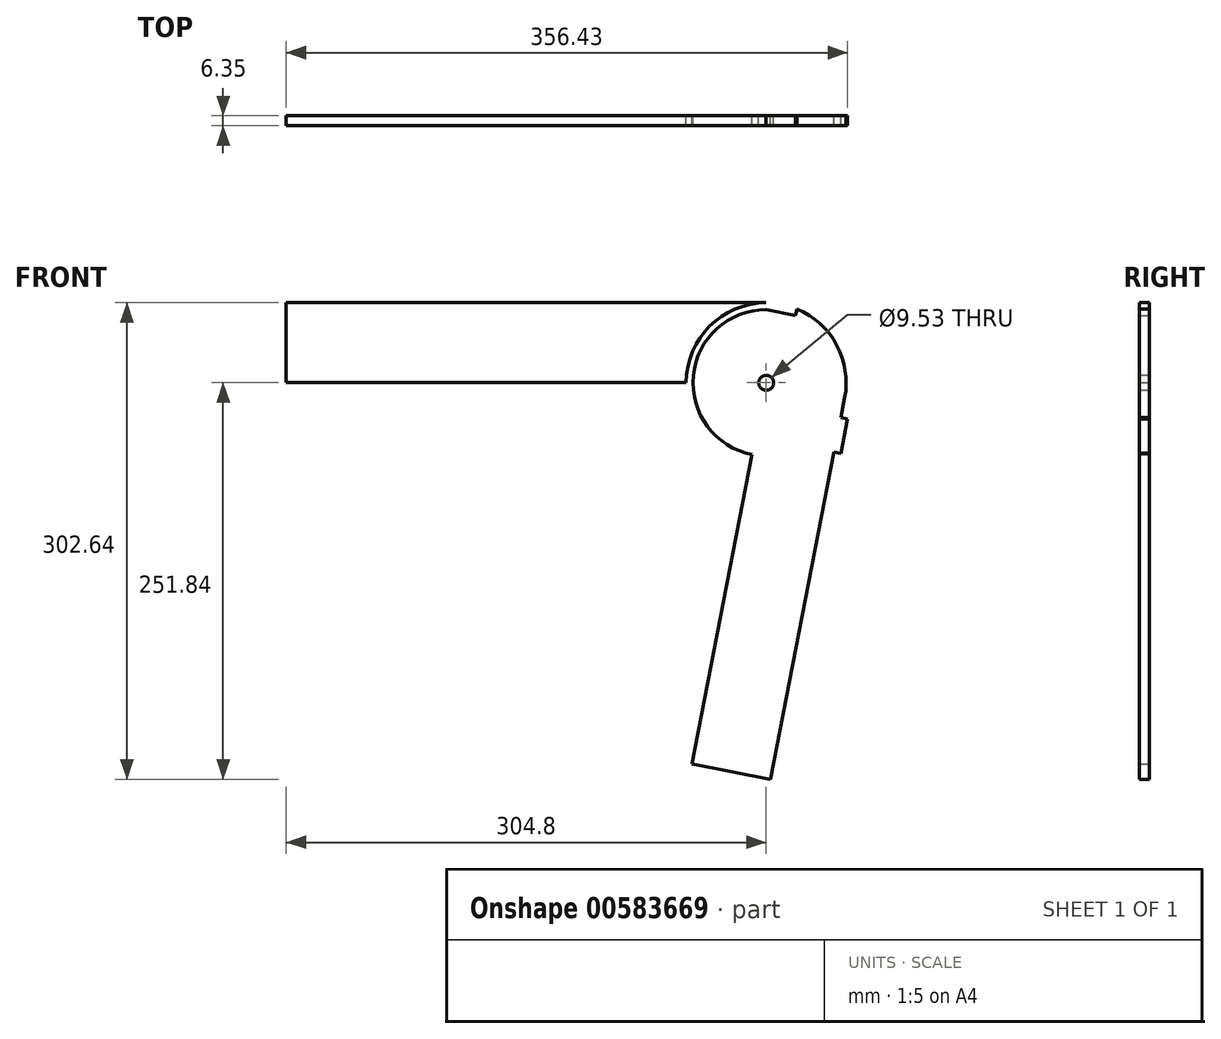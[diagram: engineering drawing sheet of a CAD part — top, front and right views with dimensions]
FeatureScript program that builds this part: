
annotation { "Feature Type Name" : "Feature", "Feature Type Description" : "" }
export const myFeature = defineFeature(function(context is Context, id is Id, definition is map)
    precondition{}
    {
        {
            var Q0;
            Q0=qCreatedBy(makeId("Front.planeOp"),FACE);
            var sketch = newSketch(context, id + "F0", { "sketchPlane" : qUnion([Q0])});
            skCircle(sketch, "E0", {"center": v(0, 0) * mm, "radius": 50.8 * mm});
            skLineSegment(sketch, "E1", {"start": v(0, 50.8) * mm, "end": v(-304.8, 50.8) * mm});
            skLineSegment(sketch, "E2", {"start": v(-304.8, 50.8) * mm, "end": v(-304.8, 0) * mm});
            skLineSegment(sketch, "E3", {"start": v(-304.8, 0) * mm, "end": v(-50.8, 0) * mm});
            skCircle(sketch, "E4", {"center": v(0, 0) * mm, "radius": 46.48 * mm});
            skCircle(sketch, "E5", {"center": v(0, 0) * mm, "radius": 4.76 * mm});
            skLineSegment(sketch, "E6", {"start": v(50.8, 0) * mm, "end": v(-50.8, 0) * mm});
            skLineSegment(sketch, "E7", {"start": v(-50.8, 0) * mm, "end": v(-50.8, -143.65) * mm});
            skLineSegment(sketch, "E8", {"start": v(0, 0) * mm, "end": v(-47.07, -242.14) * mm});
            skLineSegment(sketch, "E9", {"start": v(-47.07, -242.14) * mm, "end": v(2.8, -251.84) * mm});
            skLineSegment(sketch, "E10", {"start": v(2.8, -251.84) * mm, "end": v(49.87, -9.7) * mm});
            skLineSegment(sketch, "E11", {"start": v(0, 0) * mm, "end": v(0, 101.6) * mm});
            skLineSegment(sketch, "E12", {"start": v(0, 0) * mm, "end": v(75.55, -14.69) * mm});
            skLineSegment(sketch, "E13", {"start": v(0, 0) * mm, "end": v(2.42, 12.47) * mm});
            skLineSegment(sketch, "E14", {"start": v(46.31, -27.98) * mm, "end": v(51.63, -22.97) * mm});
            skLineSegment(sketch, "E15", {"start": v(51.63, -22.97) * mm, "end": v(47.37, -44.92) * mm});
            skLineSegment(sketch, "E16", {"start": v(47.37, -44.92) * mm, "end": v(43.18, -44.1) * mm});
            skLineSegment(sketch, "E17", {"start": v(51.63, -22.97) * mm, "end": v(47.44, -22.16) * mm});
            skLineSegment(sketch, "E18", {"start": v(0, 50.8) * mm, "end": v(0, 46.48) * mm});
            skLineSegment(sketch, "E19", {"start": v(0, 46.48) * mm, "end": v(18.65, 42.58) * mm});
            skLineSegment(sketch, "E20", {"start": v(18.65, 42.58) * mm, "end": v(19.55, 46.89) * mm});
            skSolve(sketch);
        }
        {
            var Q0;
            {var subQ0=sQuery(id+"F0.wireOp",EDGE,"E1");Q0=makeQuery(id+"F0.imprint","IMPRINT",FACE,{"disambiguationData":[TD([[makeQuery(id+"F0.imprint","IMPRINT",EDGE,{"derivedFrom":subQ0}),1.0]])]});}
            var Q1;
            {var subQ0=sQuery(id+"F0.wireOp",EDGE,"E14");Q1=makeQuery(id+"F0.imprint","IMPRINT",FACE,{"disambiguationData":[TD([[makeQuery(id+"F0.imprint","IMPRINT",EDGE,{"derivedFrom":subQ0}),-1.0]])]});}
            var Q2;
            {var subQ0=sQuery(id+"F0.wireOp",EDGE,"E14");Q2=makeQuery(id+"F0.imprint","IMPRINT",FACE,{"disambiguationData":[TD([[makeQuery(id+"F0.imprint","IMPRINT",EDGE,{"derivedFrom":subQ0}),1.0]])]});}
            var Q3;
            {var subQ3=sQuery(id+"F0.wireOp",EDGE,"E20");Q3=makeQuery(id+"F0.imprint","IMPRINT",FACE,{"disambiguationData":[TD([[makeQuery(id+"F0.imprint","IMPRINT",EDGE,{"derivedFrom":subQ3}),-1.0]])]});}
            var Q4;
            {var subQ1=sQuery(id+"F0.wireOp",EDGE,"E9");Q4=makeQuery(id+"F0.imprint","IMPRINT",FACE,{"disambiguationData":[TD([[makeQuery(id+"F0.imprint","IMPRINT",EDGE,{"derivedFrom":subQ1}),1.0]])]});}
            var Q5;
            {var subQ0=sQuery(id+"F0.wireOp",EDGE,"E6");var subQ5=sQuery(id+"F0.wireOp",EDGE,"E4");var subQ7=makeQuery(id+"F0.imprint","INTERSECT",VERTEX,{"disambiguationData":[OD(0.0)],"derivedFrom":[subQ5,subQ0]});Q5=makeQuery(id+"F0.imprint","IMPRINT",FACE,{"disambiguationData":[TD([[makeQuery(id+"F0.imprint","IMPRINT",EDGE,{"disambiguationData":[TD([[subQ7,1.0]])],"derivedFrom":subQ5}),-1.0]])]});}
            var Q6;
            {var subQ0=sQuery(id+"F0.wireOp",EDGE,"E18");Q6=makeQuery(id+"F0.imprint","IMPRINT",FACE,{"disambiguationData":[TD([[makeQuery(id+"F0.imprint","IMPRINT",EDGE,{"derivedFrom":subQ0}),-1.0]])]});}
            var Q7;
            {var subQ3=sQuery(id+"F0.wireOp",EDGE,"E8");var subQ5=sQuery(id+"F0.wireOp",EDGE,"E4");var subQ6=makeQuery(id+"F0.imprint","INTERSECT",VERTEX,{"derivedFrom":[subQ5,subQ3]});Q7=makeQuery(id+"F0.imprint","IMPRINT",FACE,{"disambiguationData":[TD([[makeQuery(id+"F0.imprint","IMPRINT",EDGE,{"disambiguationData":[TD([[subQ6,-1.0]])],"derivedFrom":subQ5}),-1.0]])]});}
            var Q8;
            {var subQ8=sQuery(id+"F0.wireOp",EDGE,"E19");Q8=makeQuery(id+"F0.imprint","IMPRINT",FACE,{"disambiguationData":[TD([[makeQuery(id+"F0.imprint","IMPRINT",EDGE,{"derivedFrom":subQ8}),-1.0]])]});}
            var Q9;
            {var subQ0=sQuery(id+"F0.wireOp",EDGE,"E11");var subQ5=sQuery(id+"F0.wireOp",EDGE,"E5");var subQ6=makeQuery(id+"F0.imprint","INTERSECT",VERTEX,{"derivedFrom":[subQ5,subQ0]});Q9=makeQuery(id+"F0.imprint","IMPRINT",FACE,{"disambiguationData":[TD([[makeQuery(id+"F0.imprint","IMPRINT",EDGE,{"disambiguationData":[TD([[subQ6,-1.0]])],"derivedFrom":subQ5}),-1.0]])]});}
            var Q10;
            {var subQ0=sQuery(id+"F0.wireOp",EDGE,"E6");var subQ1=sQuery(id+"F0.wireOp",EDGE,"E4");var subQ2=makeQuery(id+"F0.imprint","INTERSECT",VERTEX,{"disambiguationData":[OD(1.0)],"derivedFrom":[subQ1,subQ0]});Q10=makeQuery(id+"F0.imprint","IMPRINT",FACE,{"disambiguationData":[TD([[makeQuery(id+"F0.imprint","IMPRINT",EDGE,{"disambiguationData":[TD([[subQ2,-1.0]])],"derivedFrom":subQ1}),1.0]])]});}
            var Q11;
            {var subQ0=sQuery(id+"F0.wireOp",EDGE,"E8");var subQ1=sQuery(id+"F0.wireOp",EDGE,"E4");var subQ2=makeQuery(id+"F0.imprint","INTERSECT",VERTEX,{"derivedFrom":[subQ1,subQ0]});Q11=makeQuery(id+"F0.imprint","IMPRINT",FACE,{"disambiguationData":[TD([[makeQuery(id+"F0.imprint","IMPRINT",EDGE,{"disambiguationData":[TD([[subQ2,-1.0]])],"derivedFrom":subQ1}),1.0]])]});}
            var Q12;
            {var subQ0=sQuery(id+"F0.wireOp",EDGE,"E6");var subQ1=sQuery(id+"F0.wireOp",EDGE,"E4");var subQ2=makeQuery(id+"F0.imprint","INTERSECT",VERTEX,{"disambiguationData":[OD(0.0)],"derivedFrom":[subQ1,subQ0]});Q12=makeQuery(id+"F0.imprint","IMPRINT",FACE,{"disambiguationData":[TD([[makeQuery(id+"F0.imprint","IMPRINT",EDGE,{"disambiguationData":[TD([[subQ2,1.0]])],"derivedFrom":subQ1}),1.0]])]});}
            extrude(context, id + "F1", {"entities" : qUnion([Q0, Q1, Q2, Q3, Q4, Q5, Q6, Q7, Q8, Q9, Q10, Q11, Q12]), "depth" : 6.35 * mm, "offsetDistance" : 25.4 * mm});
        }
    });
